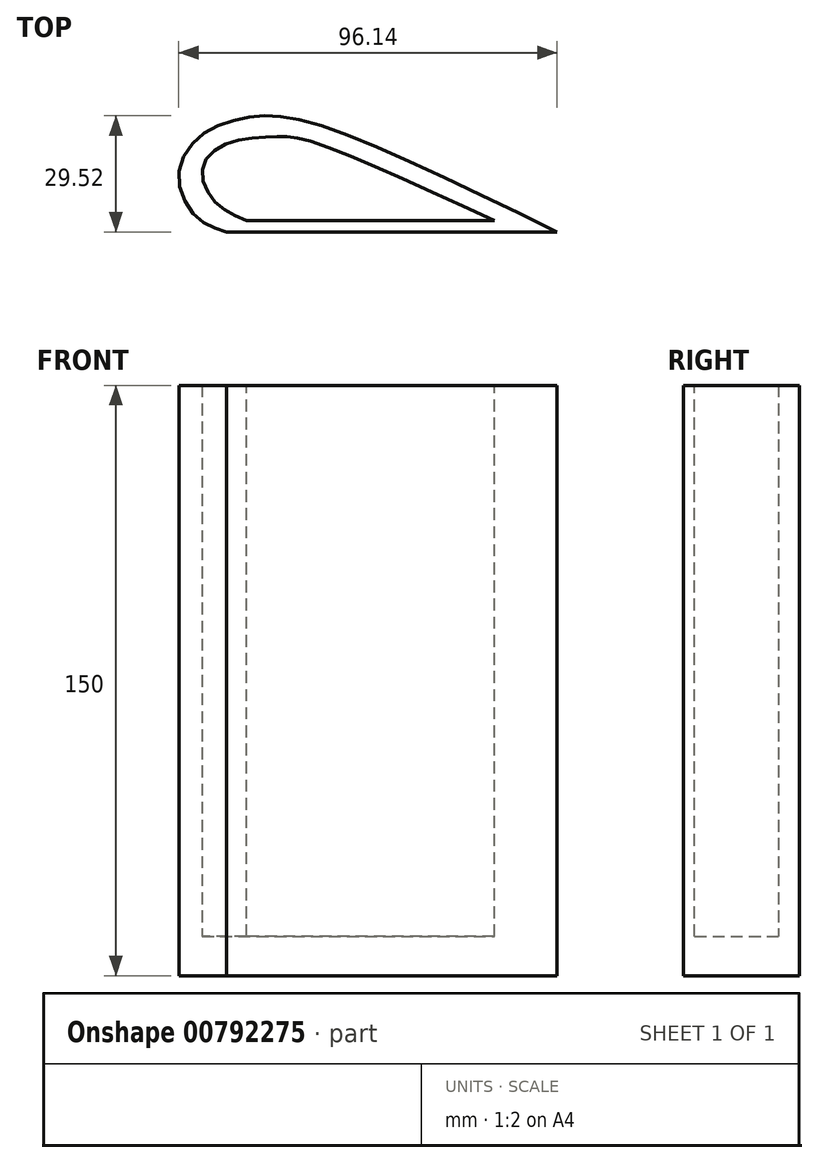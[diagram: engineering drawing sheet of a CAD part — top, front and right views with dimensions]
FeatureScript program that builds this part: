
annotation { "Feature Type Name" : "Feature", "Feature Type Description" : "" }
export const myFeature = defineFeature(function(context is Context, id is Id, definition is map)
    precondition{}
    {
        {
            var Q0;
            Q0=qCreatedBy(makeId("Top.planeOp"),FACE);
            var sketch = newSketch(context, id + "F0", { "sketchPlane" : qUnion([Q0])});
            skLineSegment(sketch, "E0", {"start": v(0, 0) * mm, "end": v(50, 0) * mm});
            skLineSegment(sketch, "E1", {"start": v(0, 0) * mm, "end": v(-20, 0) * mm});
            skFitSpline(sketch, "E2", {"points": [v(-20, 0) * mm, v(-27.4, 3.5) * mm, v(-32.14, 13.94) * mm, v(-26.64, 24.36) * mm, v(-14.5, 29.1) * mm, v(1.42, 27.78) * mm, v(64, 0) * mm], "startDerivative": vector(-69.29, 20.18) * mm, "endDerivative": vector(224.74, -110.05) * mm});
            skLineSegment(sketch, "E3", {"start": v(50, 0) * mm, "end": v(64, 0) * mm});
            skSolve(sketch);
        }
        {
            var Q0;
            Q0=makeQuery(id+"F0.imprint","IMPRINT",FACE,{"disambiguationData":[TD([[makeQuery(id+"F0.imprint","IMPRINT",EDGE,{"derivedFrom":sQuery(id+"F0.wireOp",EDGE,"E0")}),1.0]])]});
            extrude(context, id + "F1", {"entities" : qUnion([Q0]), "depth" : 150 * mm, "offsetDistance" : 25 * mm});
        }
        {
            var Q0;
            Q0=makeQuery(id+"F1.opExtrude","CAP_FACE",FACE,{"disambiguationData":[OSD([sQuery(id+"F0.wireOp",EDGE,"E0"),sQuery(id+"F0.wireOp",EDGE,"E1"),sQuery(id+"F0.wireOp",EDGE,"E2"),sQuery(id+"F0.wireOp",EDGE,"E3")])],"isStart":false});
            var sketch = newSketch(context, id + "F2", { "sketchPlane" : qUnion([Q0])});
            skLineSegment(sketch, "E4", {"start": v(0, 0) * mm, "end": v(0, 28.17) * mm, "construction": true});
            skLineSegment(sketch, "E5", {"start": v(0, 2.9) * mm, "end": v(48, 2.9) * mm});
            skLineSegment(sketch, "E6", {"start": v(0, 2.9) * mm, "end": v(-15, 2.9) * mm});
            skFitSpline(sketch, "E7", {"points": [v(-15, 2.9) * mm, v(-23.23, 7.93) * mm, v(-26.03, 16.52) * mm, v(-19.31, 22.67) * mm, v(-7.74, 24.17) * mm, v(0, 23.42) * mm, v(48, 2.9) * mm], "startDerivative": vector(-65.79, 28.3) * mm, "endDerivative": vector(183.96, -85.09) * mm});
            skSolve(sketch);
        }
        {
            var Q0;
            Q0=makeQuery(id+"F2.imprint","IMPRINT",FACE,{"disambiguationData":[TD([[makeQuery(id+"F2.imprint","IMPRINT",EDGE,{"derivedFrom":sQuery(id+"F2.wireOp",EDGE,"E5")}),1.0]])]});
            extrude(context, id + "F3", {"entities" : qUnion([Q0]), "operationType" : NewBodyOperationType.REMOVE, "oppositeDirection" : true, "depth" : 140 * mm, "offsetDistance" : 25 * mm});
        }
    });
